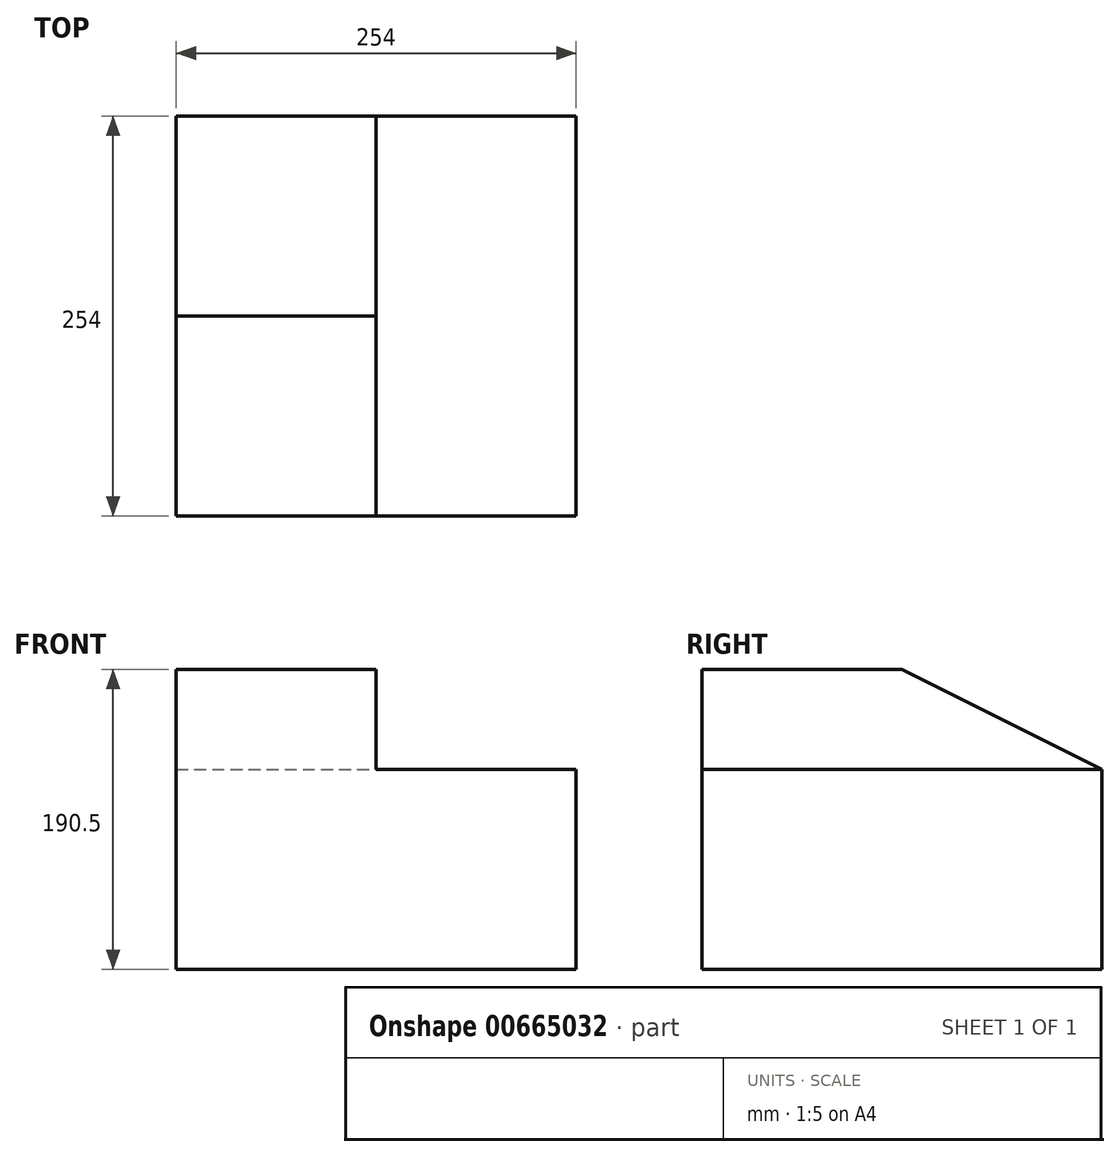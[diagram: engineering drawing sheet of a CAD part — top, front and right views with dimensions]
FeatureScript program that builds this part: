
annotation { "Feature Type Name" : "Feature", "Feature Type Description" : "" }
export const myFeature = defineFeature(function(context is Context, id is Id, definition is map)
    precondition{}
    {
        {
            var Q0;
            Q0=qCreatedBy(makeId("Front.planeOp"),FACE);
            var sketch = newSketch(context, id + "F0", { "sketchPlane" : qUnion([Q0])});
            skLineSegment(sketch, "E0", {"start": v(0, 0) * mm, "end": v(254, 0) * mm});
            skLineSegment(sketch, "E1", {"start": v(254, 0) * mm, "end": v(254, 127) * mm});
            skLineSegment(sketch, "E2", {"start": v(254, 127) * mm, "end": v(127, 127) * mm});
            skLineSegment(sketch, "E3", {"start": v(0, 0) * mm, "end": v(0, 190.5) * mm});
            skLineSegment(sketch, "E4", {"start": v(0, 190.5) * mm, "end": v(127, 190.5) * mm});
            skLineSegment(sketch, "E5", {"start": v(127, 190.5) * mm, "end": v(127, 127) * mm});
            skSolve(sketch);
        }
        {
            var Q0;
            Q0=makeQuery(id+"F0.imprint","IMPRINT",FACE,{"disambiguationData":[TD([[makeQuery(id+"F0.imprint","IMPRINT",EDGE,{"derivedFrom":sQuery(id+"F0.wireOp",EDGE,"E0")}),1.0]])]});
            extrude(context, id + "F1", {"entities" : qUnion([Q0]), "endBound" : BoundingType.SYMMETRIC, "depth" : 254 * mm, "offsetDistance" : 25.4 * mm});
        }
        {
            var Q0;
            Q0=makeQuery(id+"F1.opExtrude","SWEPT_FACE",FACE,{"disambiguationData":[OSD([sQuery(id+"F0.wireOp",EDGE,"E5")])]});
            var sketch = newSketch(context, id + "F2", { "sketchPlane" : qUnion([Q0])});
            skLineSegment(sketch, "E6", {"start": v(-127, 190.5) * mm, "end": v(0, 190.5) * mm});
            skLineSegment(sketch, "E7", {"start": v(0, 190.5) * mm, "end": v(127, 127) * mm});
            skSolve(sketch);
        }
        {
            var Q0;
            Q0 = qSketchRegion(id + "F2", true);
            var Q1;
            {var subQ0=sQuery(id+"F2.wireOp",EDGE,"E7");Q1=makeQuery(id+"F2.imprint","IMPRINT",FACE,{"disambiguationData":[TD([[makeQuery(id+"F2.imprint","IMPRINT",EDGE,{"derivedFrom":subQ0}),1.0]])]});}
            extrude(context, id + "F3", {"entities" : qUnion([Q0, Q1]), "operationType" : NewBodyOperationType.REMOVE, "oppositeDirection" : true, "depth" : 127 * mm, "offsetDistance" : 25.4 * mm});
        }
        {
            var Q0;
            Q0=makeQuery(id+"F1.opExtrude","CAP_FACE",FACE,{"disambiguationData":[OSD([sQuery(id+"F0.wireOp",EDGE,"E0"),sQuery(id+"F0.wireOp",EDGE,"E1"),sQuery(id+"F0.wireOp",EDGE,"E2"),sQuery(id+"F0.wireOp",EDGE,"E3"),sQuery(id+"F0.wireOp",EDGE,"E4"),sQuery(id+"F0.wireOp",EDGE,"E5")])],"isStart":false});
            var sketch = newSketch(context, id + "F4", { "sketchPlane" : qUnion([Q0])});
            skLineSegment(sketch, "E8", {"start": v(127, 127) * mm, "end": v(254, 0) * mm});
            skSolve(sketch);
        }
        {
            var Q0;
            Q0=makeQuery(id+"F1.opExtrude","SWEPT_EDGE",EDGE,{"disambiguationData":[OSD([sQuery(id+"F0.wireOp",EDGE,"E1"),sQuery(id+"F0.wireOp",EDGE,"E2")])]});
            cPoint(context, id + "F5", {"entities" : qUnion([Q0]), "parameter" : 0.5});
        }
        {
            var Q0;
            Q0=sQuery(id+"F4.wireOp",VERTEX,"E8.start");
            var Q1;
            Q1=sQuery(id+"F4.wireOp",VERTEX,"E8.end");
            var Q2;
            Q2 = qCreatedBy(id + "F5" ,VERTEX);
            cPlane(context, id + "F6", {"entities" : qUnion([Q0, Q1, Q2]), "cplaneType" : CPlaneType.THREE_POINT, "offset" : 25.4 * mm, "width" : 152.4 * mm, "height" : 152.4 * mm});
        }
        {
            var Q0;
            Q0=qCreatedBy(id+"F6.planeOp",FACE);
            var sketch = newSketch(context, id + "F7", { "sketchPlane" : qUnion([Q0])});
            skLineSegment(sketch, "E9", {"start": v(0, -179.6) * mm, "end": v(-155.54, -89.8) * mm});
            skLineSegment(sketch, "E10", {"start": v(0, -179.6) * mm, "end": v(0, 0) * mm});
            skLineSegment(sketch, "E11", {"start": v(-155.54, -89.8) * mm, "end": v(0, 0) * mm});
            skSolve(sketch);
        }
        {
            var Q0;
            Q0 = qSketchRegion(id + "F7", true);
            extrude(context, id + "F8", {"entities" : qUnion([Q0]), "operationType" : NewBodyOperationType.REMOVE, "oppositeDirection" : true, "depth" : 287.27 * mm, "offsetDistance" : 25.4 * mm});
        }
    });
